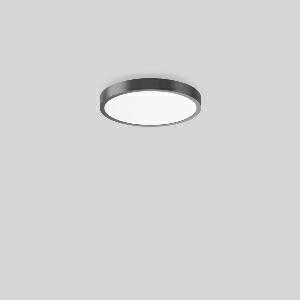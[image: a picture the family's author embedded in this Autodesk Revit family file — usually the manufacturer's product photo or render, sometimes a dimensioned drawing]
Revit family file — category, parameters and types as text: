
# Revit family: triona_round_a_312420_0031_1_76_0fd9
name_source: partatom
category: Lighting Fixtures
units: mm (PartAtom-declared; Revit-internal decimal feet)

## family parameters
Cut with Voids When Loaded = No
Host = Face
Light Source = No
Part Type = Normal
Room Calculation Point = No
Round Connector Dimension = Use Diameter
Shared = No

## types (1)
- TRIONA round A (1 x LED Modul 840, 6050 lm, 4000)
    Apparent Load = 64 VA
    CIE Flux Codes = 49 80 96 82 100
    Color Rendering = 80
    Color Temperature = 4000
    Default Elevation = 1800 mm
    Description = Series: TRIONA round
Decorative round LED surface-mounted luminaire. Flat, seamless frame: aluminium extrusion profile, powder coated. Cover made of sheet steel, powder-coated. Direct light emission through a diffuser plastic opal. Indirect light emission through a flush diffuser made of satin-finish plastic. Lightguide and diffuser made of non-yellowing plastic (PMMA). Lateral light emission (RZB SIDELITE technology) for above-average homogeneous light distribution. Direct 70%, indirect 30% light emission. Suitable for Ceiling mounting, Wall (surface). Tool-free mounting via bayonet connection. Electronic ballast included. Very easy installation thanks to Plug+Play connection. 
Colour: anthracite metallic (DB703)
Diameter: 461 mm
Height: 88 mm
Lamp: LED
Socket: without socket
Colour temperature: 4000K
Colour rendering index (CRI): 80
System power: 64 W
Rated luminous flux: 6050 lm
Luminous efficiency: 95 lm/W
Control gear: Converter, dimmable, DALI
Protection class: I
Type of protection: IP 20
    Height = 88 mm
    Lamp = 1 x LED Modul 840
    Lamp Light Flux = 6050 lm
    Lamp count = 1
    Length = 461 mm
    Lifetime = 50000 h
    Luminous efficacy = 95 lm/W
    Manufacturer = RZB
    ModVariant = No
    Model = 312420.0031.1.76
    Mounting Place = Ceiling
    Mounting Type = Surface mounted
    Number of Poles = 1
    OnlyDefault = Yes
    Power Factor = 1
    Product Name = TRIONA round A
    Product group = Surface mounted modular luminaires
    ProductGroupID = 306
    Protection Class = Protection class I
    Protection Degree = IP 20
    RLX_Detail_Level = 1
    RLX_Emergency_Light_Flux = 0 lm
    RLX_Emergency_Type = 0
    RLX_Emergency_Type_DB = No
    RlxData = <blob elided: 37549 chars, md5=66923173>
    Socket = socket
    Standby Power = 0 W
    System Light Flux = 6050 lm
    System Power = 64 W
    Type Comments = Product without accessories
    Type Image = 312420.0031.jpg
    URL = http://relux.com
    VarID = ---
    Voltage = 230 V
    Voltage Range = 220-240 V
    Weight = 0.00 kg
    Width = 0 mm  [stored 0 ft]

note: [stored X ft] marks values corroborated as IEEE doubles in the binary element streams (Revit-internal decimal feet)

## geometry (parser evidence)
native form markers: Blend x4, Sweep x11
no freeform markers — native parametric forms only
